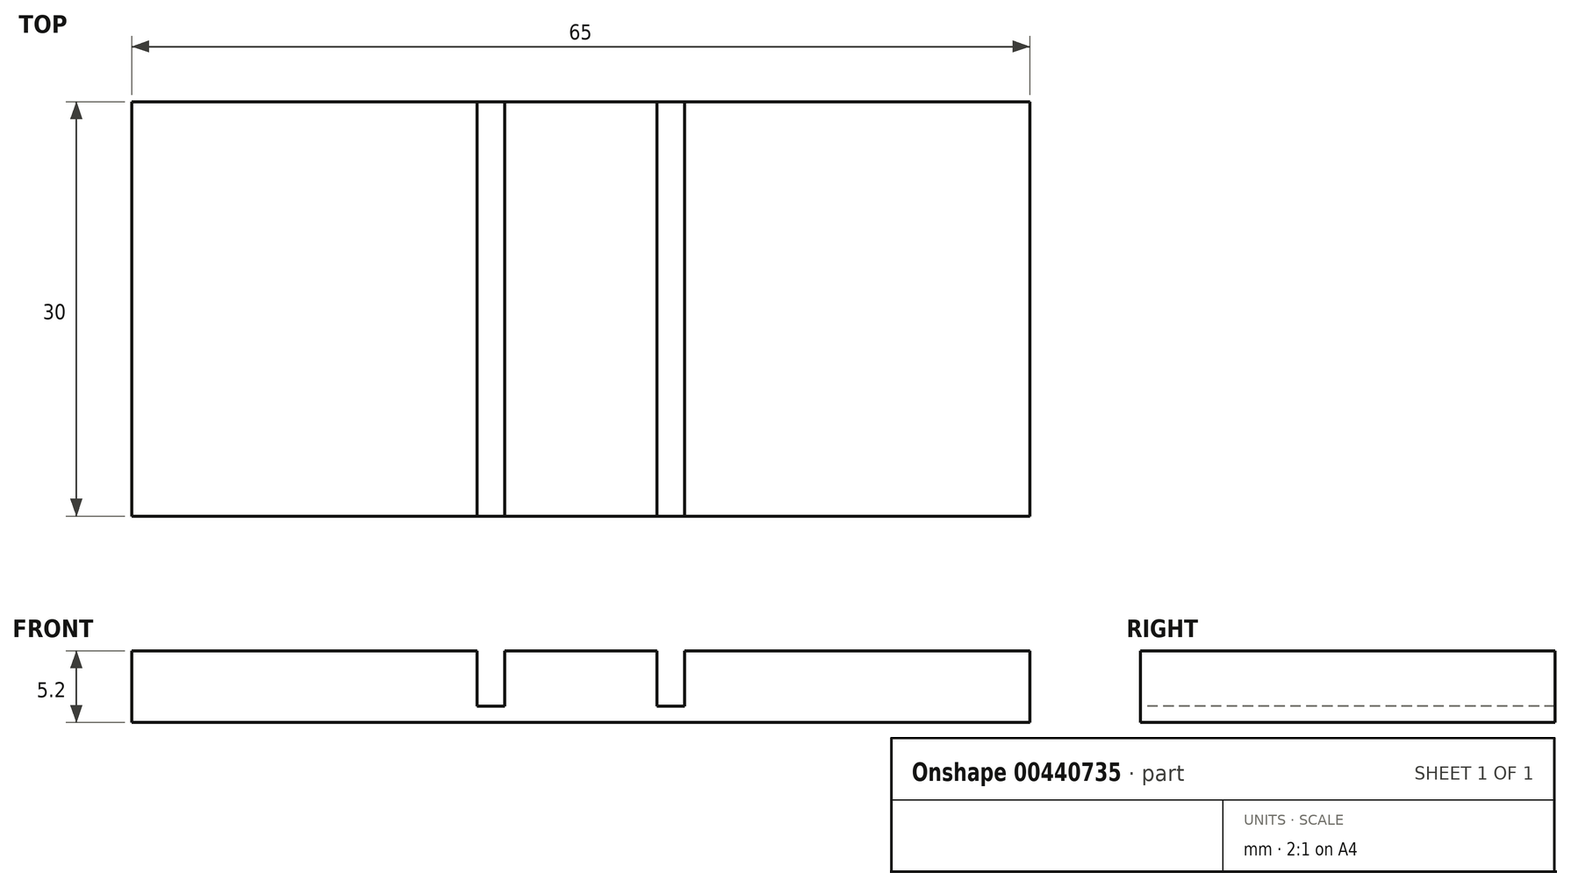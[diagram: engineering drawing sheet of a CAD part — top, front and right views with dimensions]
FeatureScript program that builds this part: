
annotation { "Feature Type Name" : "Feature", "Feature Type Description" : "" }
export const myFeature = defineFeature(function(context is Context, id is Id, definition is map)
    precondition{}
    {
        {
            var Q0;
            Q0=qCreatedBy(makeId("Top.planeOp"),FACE);
            var sketch = newSketch(context, id + "F0", { "sketchPlane" : qUnion([Q0])});
            skLineSegment(sketch, "E0.bottom", {"start": v(0, 0) * mm, "end": v(65, 0) * mm});
            skLineSegment(sketch, "E0.top", {"start": v(0, 30) * mm, "end": v(65, 30) * mm});
            skLineSegment(sketch, "E0.left", {"start": v(0, 0) * mm, "end": v(0, 30) * mm});
            skLineSegment(sketch, "E0.right", {"start": v(65, 0) * mm, "end": v(65, 30) * mm});
            skSolve(sketch);
        }
        {
            var Q0;
            Q0=makeQuery(id+"F0.imprint","IMPRINT",FACE,{"disambiguationData":[TD([[makeQuery(id+"F0.imprint","IMPRINT",EDGE,{"derivedFrom":sQuery(id+"F0.wireOp",EDGE,"E0.bottom")}),1.0]])]});
            extrude(context, id + "F1", {"entities" : qUnion([Q0]), "depth" : 1.2 * mm});
        }
        {
            var Q0;
            Q0=makeQuery(id+"F1.opExtrude","CAP_FACE",FACE,{"disambiguationData":[OSD([sQuery(id+"F0.wireOp",EDGE,"E0.bottom"),sQuery(id+"F0.wireOp",EDGE,"E0.top"),sQuery(id+"F0.wireOp",EDGE,"E0.left"),sQuery(id+"F0.wireOp",EDGE,"E0.right")])],"isStart":false});
            var sketch = newSketch(context, id + "F2", { "sketchPlane" : qUnion([Q0])});
            skLineSegment(sketch, "E1.bottom", {"start": v(0, 0) * mm, "end": v(25, 0) * mm});
            skLineSegment(sketch, "E1.top", {"start": v(0, 30) * mm, "end": v(25, 30) * mm});
            skLineSegment(sketch, "E1.left", {"start": v(0, 0) * mm, "end": v(0, 30) * mm});
            skLineSegment(sketch, "E1.right", {"start": v(25, 0) * mm, "end": v(25, 30) * mm});
            skLineSegment(sketch, "E2.bottom", {"start": v(65, 30) * mm, "end": v(40, 30) * mm});
            skLineSegment(sketch, "E2.top", {"start": v(65, 0) * mm, "end": v(40, 0) * mm});
            skLineSegment(sketch, "E2.left", {"start": v(65, 30) * mm, "end": v(65, 0) * mm});
            skLineSegment(sketch, "E2.right", {"start": v(40, 30) * mm, "end": v(40, 0) * mm});
            skLineSegment(sketch, "E3.bottom", {"start": v(27, 30) * mm, "end": v(38, 30) * mm});
            skLineSegment(sketch, "E3.top", {"start": v(27, 0) * mm, "end": v(38, 0) * mm});
            skLineSegment(sketch, "E3.left", {"start": v(27, 30) * mm, "end": v(27, 0) * mm});
            skLineSegment(sketch, "E3.right", {"start": v(38, 30) * mm, "end": v(38, 0) * mm});
            skSolve(sketch);
        }
        {
            var Q0;
            Q0 = qSketchRegion(id + "F2", true);
            extrude(context, id + "F3", {"entities" : qUnion([Q0]), "operationType" : NewBodyOperationType.ADD, "depth" : 4 * mm});
        }
    });
